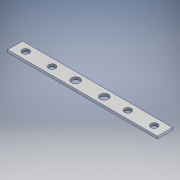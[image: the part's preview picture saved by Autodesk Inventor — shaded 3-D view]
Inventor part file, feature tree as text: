
AUTODESK INVENTOR PART (.ipt)
format: ipt  version: 2017 (Build 210142000, 142)  size: 111,104 bytes
history: native  units: mm
features: extrude x1, sketch x1
ambient origin geometry x8: Origin, YZ Plane, XZ Plane, XY Plane, X Axis, Y Axis, Z Axis, Center Point
bodies: Solid1 (feature_tree)
feature tree (2):
  extrude  "Extrusion1"  Depth=9.525mm
  sketch  "Sketch1"  dims[d4=26.0mm d6=26.0mm d8=32.0mm d10=26.0mm d12=26.0mm d14=32.0mm d16=568.96mm d17=57.15mm d18=40.64mm d19=140.776mm d20=230.152mm d21=230.152mm d22=40.64mm d23=140.776mm d24=9.525mm d25=0.0mm]
